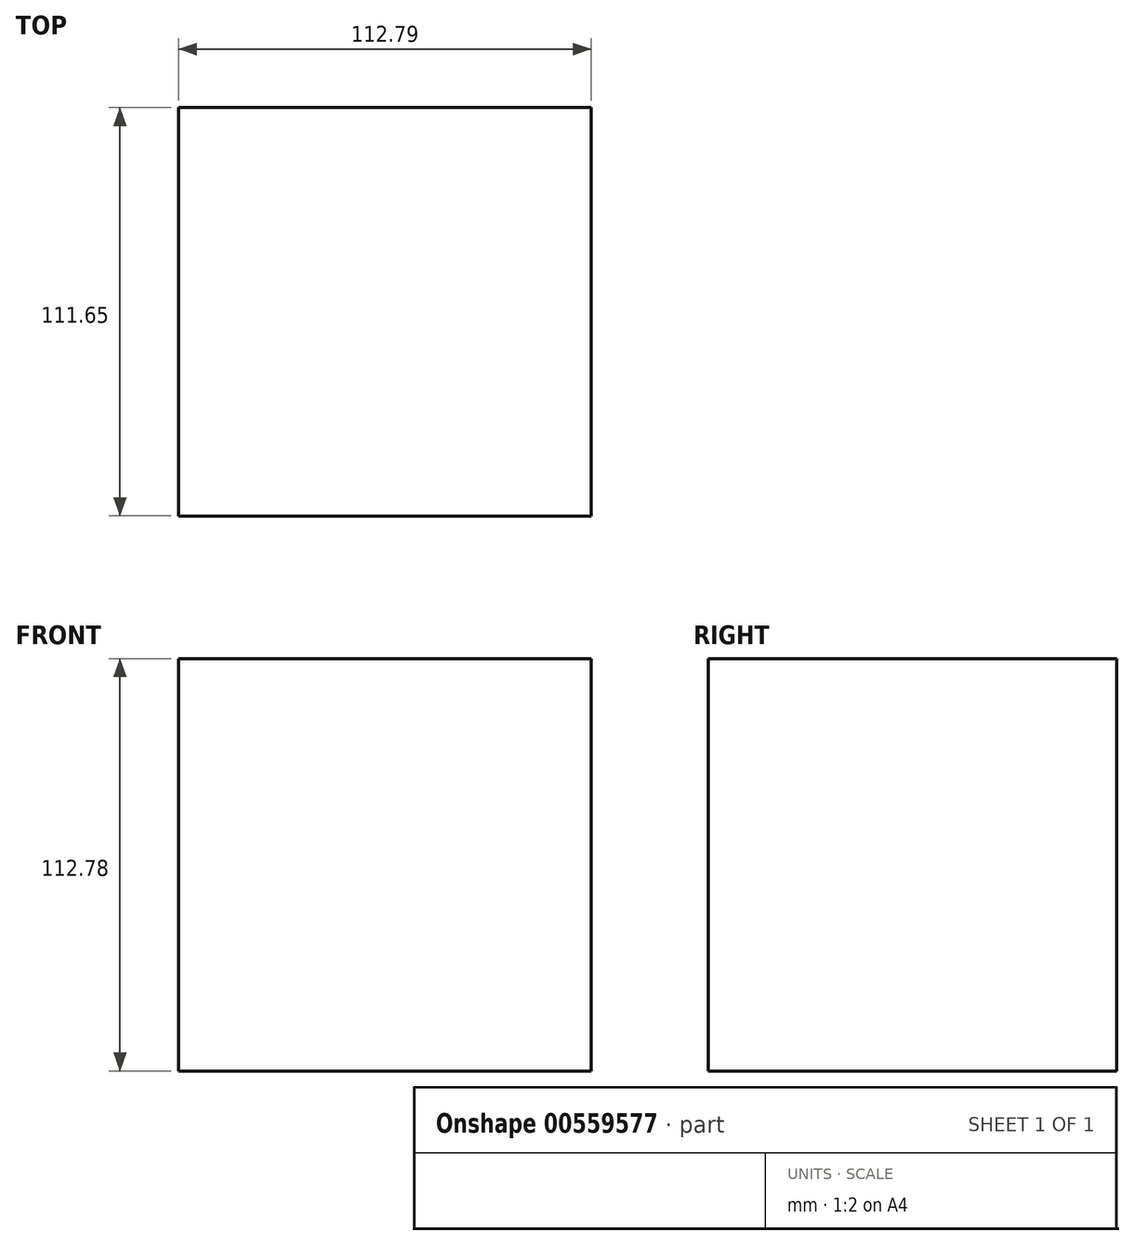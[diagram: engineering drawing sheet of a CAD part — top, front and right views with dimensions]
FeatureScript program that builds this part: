
annotation { "Feature Type Name" : "Feature", "Feature Type Description" : "" }
export const myFeature = defineFeature(function(context is Context, id is Id, definition is map)
    precondition{}
    {
        {
            var Q0;
            Q0=qCreatedBy(makeId("Top.planeOp"),FACE);
            var sketch = newSketch(context, id + "F0", { "sketchPlane" : qUnion([Q0])});
            skLineSegment(sketch, "E0", {"start": v(0, 56.4) * mm, "end": v(0, -55.26) * mm});
            skLineSegment(sketch, "E1", {"start": v(0, -55.26) * mm, "end": v(0, 0) * mm});
            skLineSegment(sketch, "E2", {"start": v(0, 0) * mm, "end": v(56.3, 0) * mm});
            skLineSegment(sketch, "E3", {"start": v(56.3, 0) * mm, "end": v(0, 0) * mm});
            skLineSegment(sketch, "E4", {"start": v(-3.78, 0) * mm, "end": v(0, 0) * mm});
            skLineSegment(sketch, "E5", {"start": v(0, 0) * mm, "end": v(-56.49, 0) * mm});
            skLineSegment(sketch, "E6", {"start": v(-56.49, 0) * mm, "end": v(-56.49, 56.4) * mm});
            skLineSegment(sketch, "E7", {"start": v(-56.49, 56.4) * mm, "end": v(0, 56.4) * mm});
            skLineSegment(sketch, "E8", {"start": v(56.3, 56.4) * mm, "end": v(56.3, 0) * mm});
            skLineSegment(sketch, "E9", {"start": v(56.3, 56.4) * mm, "end": v(0, 56.4) * mm});
            skLineSegment(sketch, "E10", {"start": v(0, -55.26) * mm, "end": v(-56.49, -55.26) * mm});
            skLineSegment(sketch, "E11", {"start": v(-56.49, -55.26) * mm, "end": v(-56.49, 0) * mm});
            skLineSegment(sketch, "E12", {"start": v(0, -55.26) * mm, "end": v(56.3, -55.26) * mm});
            skLineSegment(sketch, "E13", {"start": v(56.3, -55.26) * mm, "end": v(56.3, 0) * mm});
            skSolve(sketch);
        }
        {
            var Q0;
            Q0 = qSketchRegion(id + "F0", true);
            extrude(context, id + "F1", {"entities" : qUnion([Q0]), "depth" : 112.78 * mm, "offsetDistance" : 25.4 * mm});
        }
    });
